# Revit family: Doppelhalter MD
name_source: partatom
category: HLS-Bauteile
revit_build: Autodesk Revit 2017 (Build: 20190507_1515(x64)
units: mm (PartAtom-declared; Revit-internal decimal feet)

## family parameters
Arbeitsebenenbasiert = Ja
Beim Laden mit Abzugskörper schneiden = Nein
Bemaßung runder Anschluss = Durchmesser verwenden
Gemeinsam genutzt = Ja
Immer vertikal = Nein
Raumberechnungspunkt = Nein
Teiletyp = Normal

## types (2) — shared parameters
B = 16 mm  [stored 0.0524934 ft]
Breite = 16 mm  [stored 0.0524934 ft]
Fabrikat = MEFA
Firma = MEFA Befestigungs- und Montagesysteme GmbH
Gewindestifttyp = M8x20
H = 20 mm  [stored 0.0656168 ft]
Höhe = 20 mm
Kurztext1 = Doppelhalter mit Gewindestift
Material = Stahl
Materialname = S235
Mengeneinheit = St
Oberflaeche = galvanisch verzinkt
Vorgabe-Ansicht = 1219 mm
max. zul. Last Zug = 0.20 kN
vpe = 50 St

## per-type parameters (varying)
| type | Achsabstand | Artikelnummer | EAN | Gewicht | Gewicht pro Bauteil | Kurztext2 | L | LG | Länge |
| Doppelhalter MD M 8, L= 65 | 65 mm | 0760048 | 4250928417343 | 0.07 kg | 0.07 kg | Achsabstand L 65 mm | 65 mm  [stored 0.213255 ft] | 85 mm  [stored 0.278871 ft] | 85 mm  [stored 0.278871 ft] |
| Doppelhalter MD M 8, L=105 | 105 mm | 0760056 | 4250928417350 | 0.09 kg | 0.09 kg | Achsabstand L 105 mm | 105 mm  [stored 0.344488 ft] | 125 mm  [stored 0.410105 ft] | 125 mm  [stored 0.410105 ft] |

note: [stored X ft] marks values corroborated as IEEE doubles in the binary element streams (Revit-internal decimal feet)
